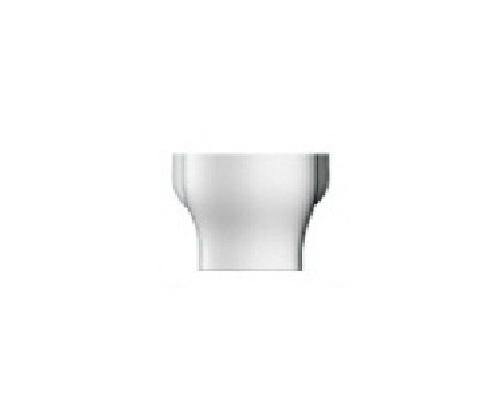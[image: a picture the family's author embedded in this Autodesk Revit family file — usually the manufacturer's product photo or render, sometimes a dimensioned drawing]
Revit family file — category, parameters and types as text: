
# Revit family: CITY ALPHABET letter „DOT”
name_source: partatom
category: Furniture
revit_build: Autodesk Revit 2018 (Build: 20190510_1515(x64)
units: mm (PartAtom-declared; Revit-internal decimal feet)

## family parameters
Cut with Voids When Loaded = No
Host = Face
OmniClass Number = 23.40.10.11.14
OmniClass Title = Exterior Seating
Room Calculation Point = No
Shared = No

## types (1)
- CITY ALPHABET letter „DOT”
    Default Elevation = 1219 mm
    Height = 340 mm  [stored 1.11549 ft]
    IfcExportAs = IfcFurnishingElement
    Length = 550 mm
    Manufacturer = Astrini Design
    Material information = Colour choice from RAL colour standard. Customer may inquire about specific request regarding individual order.
    Model = CITY ALPHABET letter „DOT”
    Operating temperature = -40°C to 80°C, ( -40°F to 176°F )
    Type Comments = Bench
    Type Image = Dot.jpg
    URL = https://astrini-design.pl
    Weight (approximately) = 11.00 kg
    Weight - filled (approximately) = 41.00 kg
    Width = 720 mm  [stored 2.3622 ft]

note: [stored X ft] marks values corroborated as IEEE doubles in the binary element streams (Revit-internal decimal feet)
